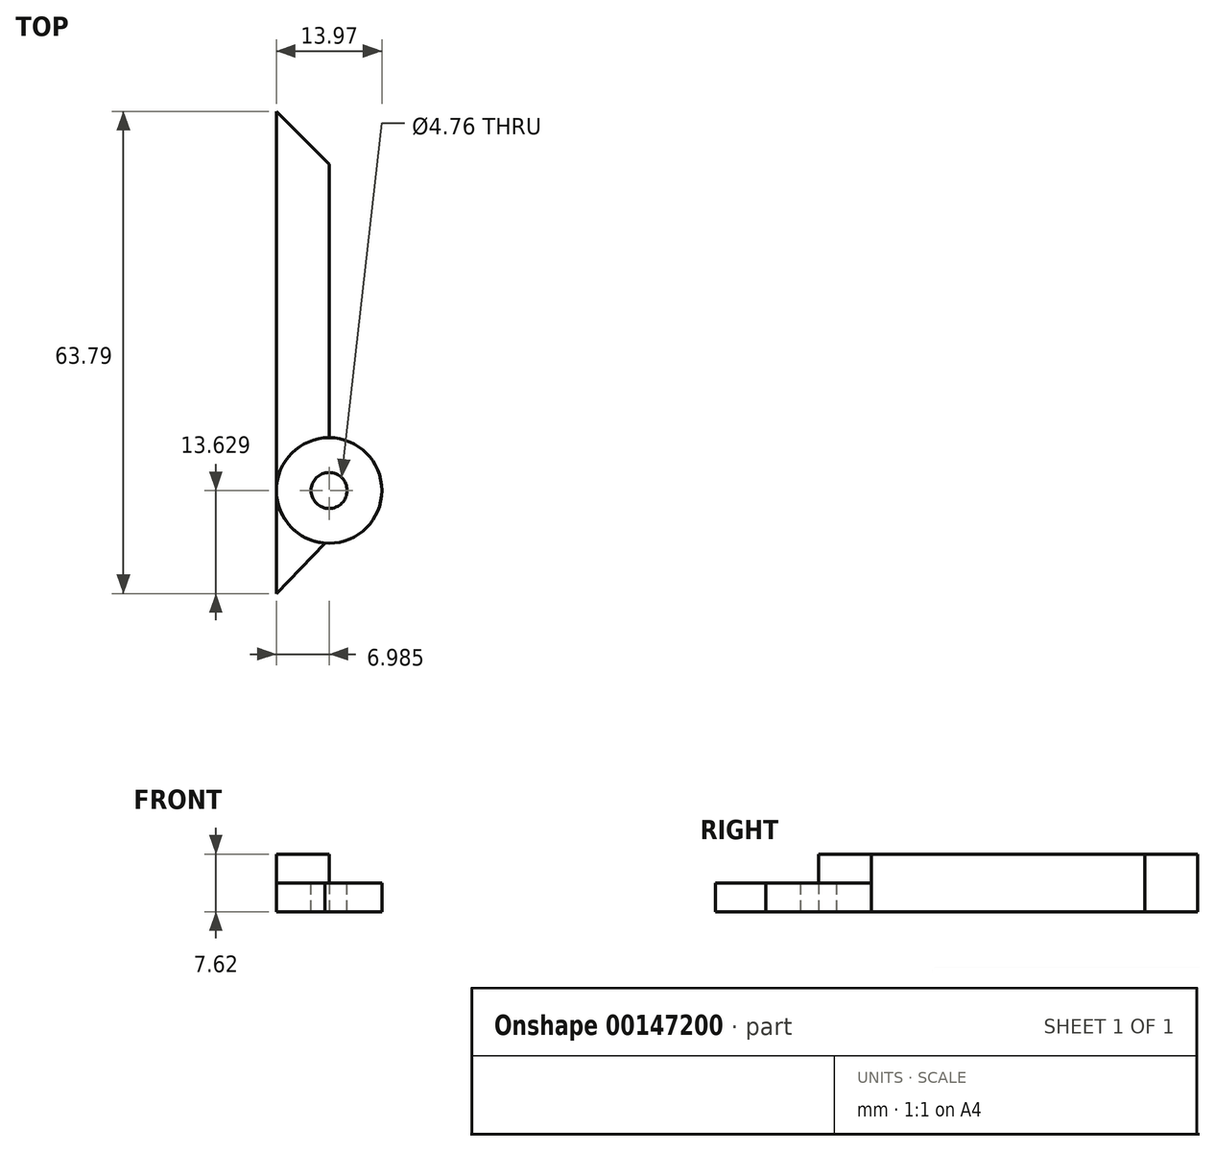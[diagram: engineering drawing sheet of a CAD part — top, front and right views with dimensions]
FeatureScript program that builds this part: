
annotation { "Feature Type Name" : "Feature", "Feature Type Description" : "" }
export const myFeature = defineFeature(function(context is Context, id is Id, definition is map)
    precondition{}
    {
        {
            var Q0;
            Q0=qCreatedBy(makeId("Top.planeOp"),FACE);
            var sketch = newSketch(context, id + "F0", { "sketchPlane" : qUnion([Q0])});
            skLineSegment(sketch, "E0.bottom", {"start": v(0, 27.42) * mm, "end": v(6.99, 27.42) * mm});
            skLineSegment(sketch, "E0.top", {"start": v(0, -23.38) * mm, "end": v(6.99, -23.38) * mm});
            skLineSegment(sketch, "E0.left", {"start": v(0, 27.42) * mm, "end": v(0, -23.38) * mm});
            skLineSegment(sketch, "E0.right", {"start": v(6.99, 27.42) * mm, "end": v(6.99, -23.38) * mm});
            skCircle(sketch, "E1", {"center": v(6.99, -23.38) * mm, "radius": 6.99 * mm});
            skSolve(sketch);
        }
        {
            var Q0;
            Q0 = qSketchRegion(id + "F0", true);
            extrude(context, id + "F1", {"entities" : qUnion([Q0]), "depth" : 7.62 * mm});
        }
        {
            var Q0;
            Q0=makeQuery(id+"F1.opExtrude","CAP_FACE",FACE,{"disambiguationData":[OSD([sQuery(id+"F0.wireOp",EDGE,"E0.bottom"),sQuery(id+"F0.wireOp",EDGE,"E0.left"),sQuery(id+"F0.wireOp",EDGE,"E0.right"),sQuery(id+"F0.wireOp",EDGE,"E1")])],"isStart":false});
            var sketch = newSketch(context, id + "F2", { "sketchPlane" : qUnion([Q0])});
            skCircle(sketch, "E2", {"center": v(6.99, -23.38) * mm, "radius": 6.99 * mm});
            skSolve(sketch);
        }
        {
            var Q0;
            {var subQ0=sQuery(id+"F2.wireOp",EDGE,"E2");var subQ1=makeQuery(id+"F2.imprint","INTERSECT",VERTEX,{"derivedFrom":[makeQuery(id+"F1.opExtrude","CAP_EDGE",EDGE,{"disambiguationData":[OSD([sQuery(id+"F0.wireOp",EDGE,"E0.left")])],"isStart":false}),subQ0]});Q0=makeQuery(id+"F2.imprint","IMPRINT",FACE,{"disambiguationData":[TD([[makeQuery(id+"F2.imprint","IMPRINT",EDGE,{"disambiguationData":[TD([[subQ1,1.0]])],"derivedFrom":subQ0}),1.0]])]});}
            extrude(context, id + "F3", {"entities" : qUnion([Q0]), "operationType" : NewBodyOperationType.REMOVE, "oppositeDirection" : true, "depth" : 3.8 * mm});
        }
        {
            var Q0;
            Q0=makeQuery(id+"F1.opExtrude","CAP_FACE",FACE,{"disambiguationData":[OSD([sQuery(id+"F0.wireOp",EDGE,"E0.bottom"),sQuery(id+"F0.wireOp",EDGE,"E0.left"),sQuery(id+"F0.wireOp",EDGE,"E0.right"),sQuery(id+"F0.wireOp",EDGE,"E1")])],"isStart":true});
            var sketch = newSketch(context, id + "F4", { "sketchPlane" : qUnion([Q0])});
            skLineSegment(sketch, "E3", {"start": v(0, 23.38) * mm, "end": v(0, 37) * mm});
            skLineSegment(sketch, "E4", {"start": v(0, 37) * mm, "end": v(6.45, 30.35) * mm});
            skSolve(sketch);
        }
        {
            var Q0;
            {var subQ0=sQuery(id+"F4.wireOp",EDGE,"E3");Q0=makeQuery(id+"F4.imprint","IMPRINT",FACE,{"disambiguationData":[TD([[makeQuery(id+"F4.imprint","IMPRINT",EDGE,{"derivedFrom":subQ0}),-1.0]])]});}
            extrude(context, id + "F5", {"entities" : qUnion([Q0]), "oppositeDirection" : true, "depth" : 3.8 * mm});
        }
        {
            var Q0;
            Q0=makeQuery(id+"F3.boolean.opBoolean","COPY",FACE,{"derivedFrom":makeQuery(id+"F3.opExtrude","CAP_FACE",FACE,{"disambiguationData":[OSD([sQuery(id+"F2.wireOp",EDGE,"E2")])],"isStart":false})});
            var sketch = newSketch(context, id + "F6", { "sketchPlane" : qUnion([Q0])});
            skPoint(sketch, "E5", {"position": v(6.99, -23.38) * mm});
            skSolve(sketch);
        }
        {
            var Q0;
            Q0=sQuery(id+"F6.wireOp",VERTEX,"E5");
            var Q1;
            Q1=makeQuery(id+"F1.opExtrude","SWEPT_BODY",BODY,{"disambiguationData":[OSD([sQuery(id+"F0.wireOp",EDGE,"E0.bottom"),sQuery(id+"F0.wireOp",EDGE,"E0.left"),sQuery(id+"F0.wireOp",EDGE,"E0.right"),sQuery(id+"F0.wireOp",EDGE,"E1")])]});
            hole(context, id + "F7", {"style" : HoleStyle.SIMPLE, "endStyle" : HoleEndStyle.BLIND, "holeDiameter" : 4.76 * mm, "holeDepth" : 12.7 * mm, "locations" : qUnion([Q0]), "scope" : qUnion([Q1])});
        }
        {
            var Q0;
            Q0=makeQuery(id+"F1.opExtrude","SWEPT_EDGE",EDGE,{"disambiguationData":[OSD([sQuery(id+"F0.wireOp",EDGE,"E0.bottom"),sQuery(id+"F0.wireOp",EDGE,"E0.right")])]});
            chamfer(context, id + "F8", {"entities" : qUnion([Q0]), "width" : 7.62 * mm, "tangentPropagation" : true});
        }
    });
